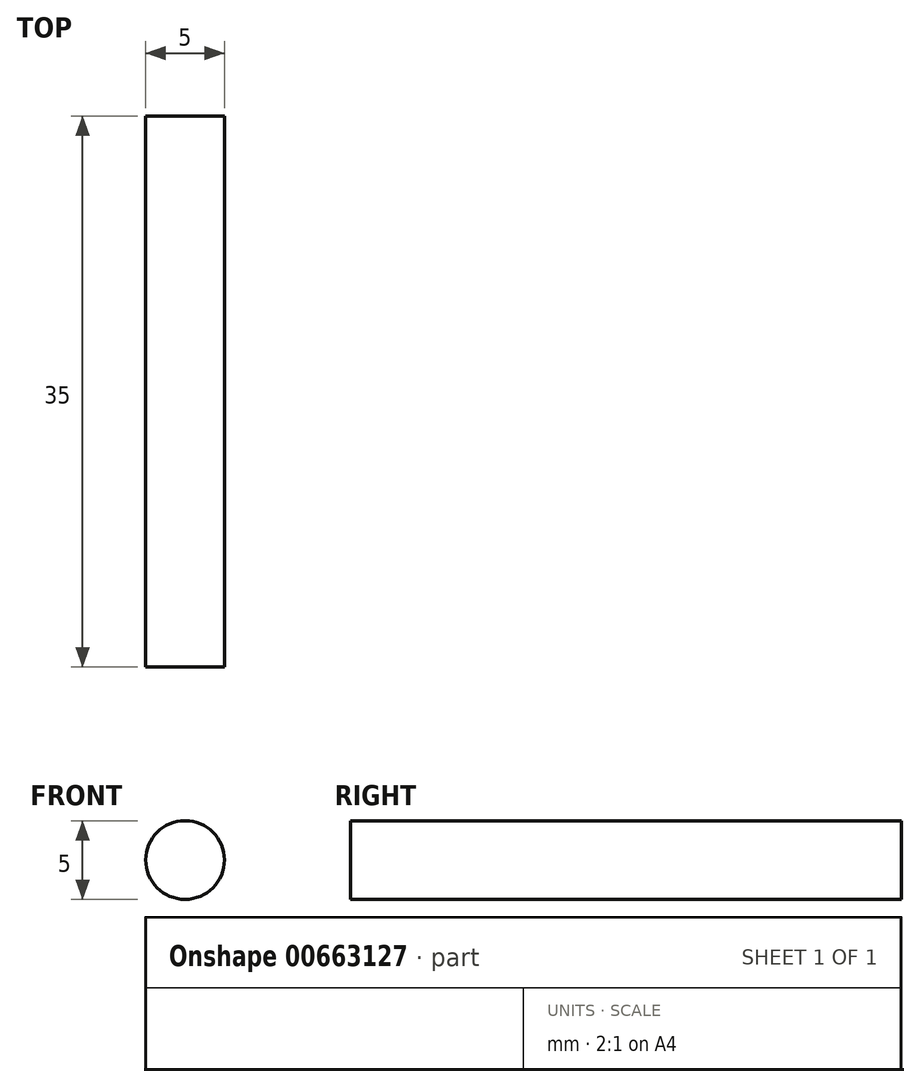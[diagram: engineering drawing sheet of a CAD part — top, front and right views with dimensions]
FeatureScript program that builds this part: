
annotation { "Feature Type Name" : "Feature", "Feature Type Description" : "" }
export const myFeature = defineFeature(function(context is Context, id is Id, definition is map)
    precondition{}
    {
        {
            var Q0;
            Q0=qCreatedBy(makeId("Front.planeOp"),FACE);
            var sketch = newSketch(context, id + "F0", { "sketchPlane" : qUnion([Q0])});
            skCircle(sketch, "E0", {"center": v(0, 0) * mm, "radius": 2.5 * mm});
            skSolve(sketch);
        }
        {
            var Q0;
            Q0=makeQuery(id+"F0.imprint","IMPRINT",FACE,{"disambiguationData":[TD([[makeQuery(id+"F0.imprint","IMPRINT",EDGE,{"derivedFrom":sQuery(id+"F0.wireOp",EDGE,"E0")}),1.0]])]});
            extrude(context, id + "F1", {"entities" : qUnion([Q0]), "depth" : 35 * mm, "offsetDistance" : 25 * mm});
        }
    });
